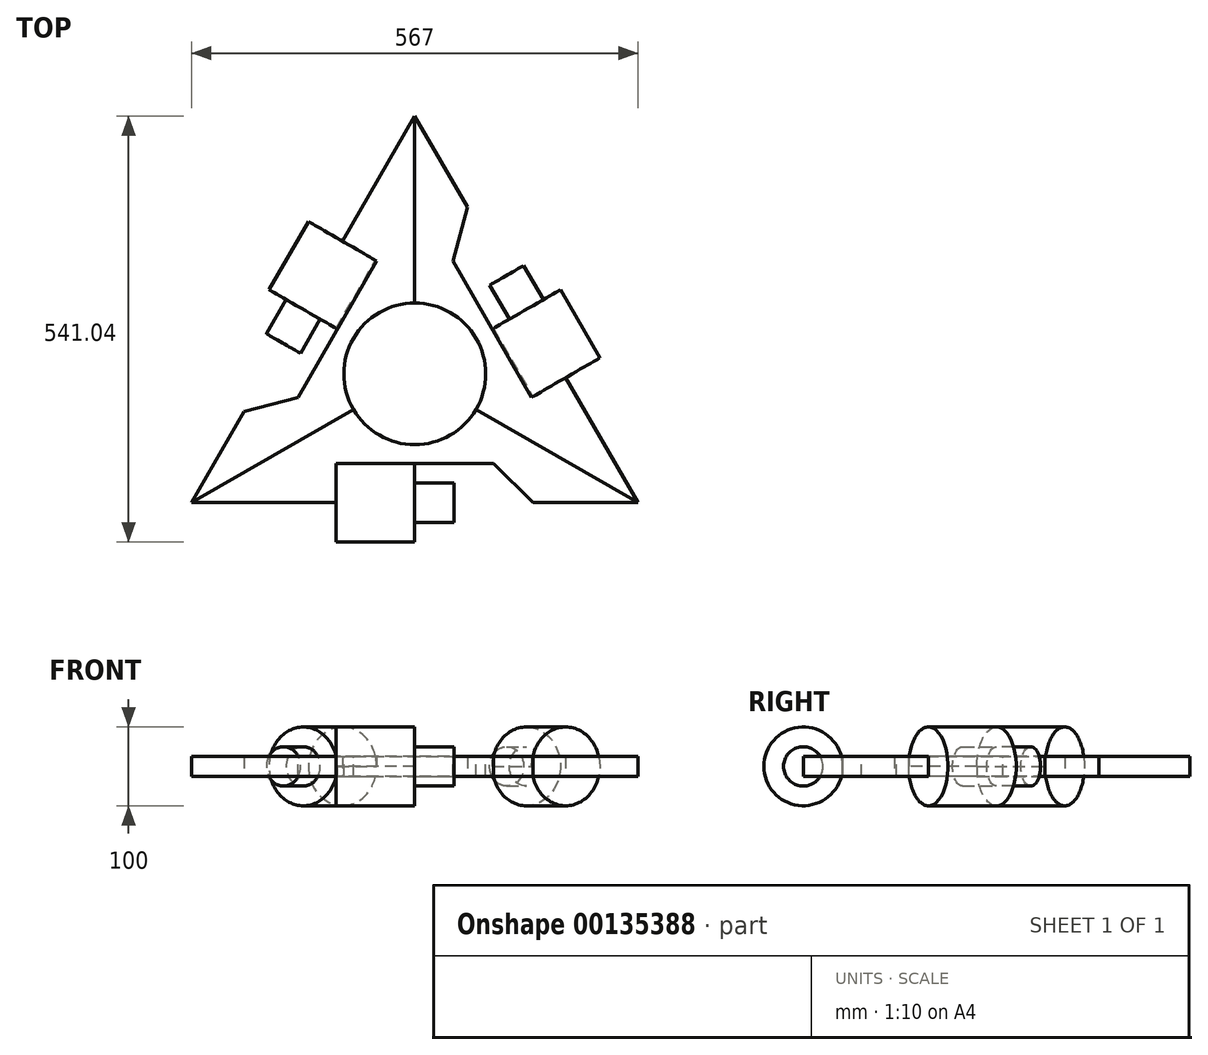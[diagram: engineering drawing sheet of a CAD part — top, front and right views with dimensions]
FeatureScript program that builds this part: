
annotation { "Feature Type Name" : "Feature", "Feature Type Description" : "" }
export const myFeature = defineFeature(function(context is Context, id is Id, definition is map)
    precondition{}
    {
        {
            var Q0;
            Q0=qCreatedBy(makeId("Top.planeOp"),FACE);
            var sketch = newSketch(context, id + "F0", { "sketchPlane" : qUnion([Q0])});
            skLineSegment(sketch, "E0", {"start": v(0, 0) * mm, "end": v(567, 0) * mm});
            skLineSegment(sketch, "E1", {"start": v(0, 0) * mm, "end": v(283.5, 491.04) * mm});
            skLineSegment(sketch, "E2", {"start": v(283.5, 491.04) * mm, "end": v(567, 0) * mm});
            skPoint(sketch, "E3", {"position": v(283.5, 491.04) * mm});
            skPoint(sketch, "E4", {"position": v(0, 0) * mm});
            skPoint(sketch, "E5", {"position": v(567, 0) * mm});
            skArc(sketch, "E6", {"start": v(567, 0) * mm, "mid": v(283.5, 491.04) * mm, "end": v(0, 0) * mm});
            skArc(sketch, "E7", {"start": v(283.5, 491.04) * mm, "mid": v(0, 0) * mm, "end": v(567, 0) * mm});
            skArc(sketch, "E8", {"start": v(0, 0) * mm, "mid": v(567, 0) * mm, "end": v(283.5, 491.04) * mm});
            skSolve(sketch);
        }
        {
            var Q0;
            Q0=makeQuery(id+"F0.imprint","IMPRINT",FACE,{"disambiguationData":[TD([[makeQuery(id+"F0.imprint","IMPRINT",EDGE,{"derivedFrom":sQuery(id+"F0.wireOp",EDGE,"E0")}),1.0]])]});
            extrude(context, id + "F1", {"entities" : qUnion([Q0]), "depth" : 25 * mm});
        }
        {
            var Q0;
            Q0=makeQuery(id+"F1.opExtrude","SWEPT_FACE",FACE,{"disambiguationData":[OSD([sQuery(id+"F0.wireOp",EDGE,"E0")])]});
            var sketch = newSketch(context, id + "F2", { "sketchPlane" : qUnion([Q0])});
            skLineSegment(sketch, "E9", {"start": v(0, 0) * mm, "end": v(567, 0) * mm});
            skLineSegment(sketch, "E10", {"start": v(283.5, 0) * mm, "end": v(283.5, 25) * mm});
            skLineSegment(sketch, "E11", {"start": v(283.5, 25) * mm, "end": v(383.5, 25) * mm});
            skLineSegment(sketch, "E12", {"start": v(383.5, 25) * mm, "end": v(383.5, 0) * mm});
            skLineSegment(sketch, "E13", {"start": v(383.5, 0) * mm, "end": v(283.5, 0) * mm});
            skLineSegment(sketch, "E14.bottom", {"start": v(283.5, 25) * mm, "end": v(183.5, 25) * mm});
            skLineSegment(sketch, "E14.top", {"start": v(283.5, 0) * mm, "end": v(183.5, 0) * mm});
            skLineSegment(sketch, "E14.left", {"start": v(283.5, 25) * mm, "end": v(283.5, 0) * mm});
            skLineSegment(sketch, "E14.right", {"start": v(183.5, 25) * mm, "end": v(183.5, 0) * mm});
            skSolve(sketch);
        }
        {
            var Q0;
            Q0=qSketchRegion(id+"F2",true);
            extrude(context, id + "F3", {"entities" : qUnion([Q0]), "operationType" : NewBodyOperationType.REMOVE, "oppositeDirection" : true, "depth" : 50 * mm});
        }
        {
            var Q0;
            Q0=makeQuery(id+"F3.boolean.opBoolean","COPY",FACE,{"derivedFrom":makeQuery(id+"F3.opExtrude","SWEPT_FACE",FACE,{"disambiguationData":[OSD([sQuery(id+"F2.wireOp",EDGE,"E14.right")])]})});
            var sketch = newSketch(context, id + "F4", { "sketchPlane" : qUnion([Q0])});
            skLineSegment(sketch, "E15", {"start": v(0, 0) * mm, "end": v(50, 0) * mm});
            skLineSegment(sketch, "E16", {"start": v(50, 0) * mm, "end": v(50, 25) * mm});
            skLineSegment(sketch, "E17", {"start": v(50, 12.5) * mm, "end": v(0, 12.5) * mm});
            skCircle(sketch, "E18", {"center": v(0, 12.5) * mm, "radius": 50 * mm});
            skSolve(sketch);
        }
        {
            var Q0;
            Q0=qSketchRegion(id+"F4",true);
            var Q1;
            {var subQ0=sQuery(id+"F2.wireOp",EDGE,"E14.right");var subQ1=makeQuery(id+"F3.boolean.opBoolean","COPY",EDGE,{"derivedFrom":makeQuery(id+"F3.opExtrude","CAP_EDGE",EDGE,{"disambiguationData":[OSD([subQ0])],"isStart":true})});var subQ7=sQuery(id+"F4.wireOp",EDGE,"E15");var subQ9=makeQuery(id+"F4.imprint","INTERSECT",VERTEX,{"derivedFrom":[subQ1,subQ7]});Q1=makeQuery(id+"F4.imprint","IMPRINT",FACE,{"disambiguationData":[TD([[makeQuery(id+"F4.imprint","IMPRINT",EDGE,{"disambiguationData":[TD([[subQ9,1.0]])],"derivedFrom":subQ7}),1.0]])]});}
            extrude(context, id + "F5", {"entities" : qUnion([Q0, Q1]), "operationType" : NewBodyOperationType.ADD, "depth" : 100 * mm});
        }
        {
            var Q0;
            Q0=makeQuery(id+"F5.opExtrude","CAP_FACE",FACE,{"disambiguationData":[OSD([sQuery(id+"F4.wireOp",EDGE,"E15"),sQuery(id+"F4.wireOp",EDGE,"E16"),sQuery(id+"F4.wireOp",EDGE,"E18")])],"isStart":false});
            var sketch = newSketch(context, id + "F6", { "sketchPlane" : qUnion([Q0])});
            skCircle(sketch, "E19", {"center": v(0, 12.5) * mm, "radius": 25 * mm});
            skSolve(sketch);
        }
        {
            var Q0;
            Q0=qSketchRegion(id+"F6",true);
            extrude(context, id + "F7", {"entities" : qUnion([Q0]), "operationType" : NewBodyOperationType.ADD, "depth" : 50 * mm});
        }
        {
            var Q0;
            Q0=makeQuery(id+"F3.boolean.opBoolean","COPY",FACE,{"derivedFrom":makeQuery(id+"F3.opExtrude","SWEPT_FACE",FACE,{"disambiguationData":[OSD([sQuery(id+"F2.wireOp",EDGE,"E12")])]})});
            extrude(context, id + "F8", {"entities" : qUnion([Q0]), "operationType" : NewBodyOperationType.REMOVE, "oppositeDirection" : true, "depth" : 50 * mm});
        }
        {
            var Q0;
            {var subQ0=sQuery(id+"F2.wireOp",EDGE,"E12");Q0=makeQuery(id+"F8.boolean.opBoolean","COPY",EDGE,{"derivedFrom":makeQuery(id+"F8.opExtrude","CAP_EDGE",EDGE,{"disambiguationData":[OSD([subQ0]),TDD([makeQuery(id+"F3.boolean.opBoolean","COPY",EDGE,{"derivedFrom":makeQuery(id+"F3.opExtrude","CAP_EDGE",EDGE,{"disambiguationData":[OSD([subQ0])],"isStart":true})})])],"isStart":false})});}
            chamfer(context, id + "F9", {"entities" : qUnion([Q0]), "width" : 50 * mm, "tangentPropagation" : true});
        }
        {
            var Q0;
            Q0=makeQuery(id+"F1.opExtrude","CAP_FACE",FACE,{"disambiguationData":[OSD([sQuery(id+"F0.wireOp",EDGE,"E0"),sQuery(id+"F0.wireOp",EDGE,"E1"),sQuery(id+"F0.wireOp",EDGE,"E2")])],"isStart":false});
            var sketch = newSketch(context, id + "F10", { "sketchPlane" : qUnion([Q0])});
            skLineSegment(sketch, "E20", {"start": v(567, 0) * mm, "end": v(141.75, 245.52) * mm});
            skLineSegment(sketch, "E21", {"start": v(0, 0) * mm, "end": v(425.25, 245.52) * mm});
            skCircle(sketch, "E22", {"center": v(283.5, 163.68) * mm, "radius": 90 * mm});
            skSolve(sketch);
        }
        {
            var Q0;
            Q0=qSketchRegion(id+"F10",true);
            var Q1;
            {var subQ1=makeQuery(id+"F1.opExtrude","CAP_EDGE",EDGE,{"disambiguationData":[OSD([sQuery(id+"F0.wireOp",EDGE,"E1")])],"isStart":false});var subQ3=sQuery(id+"F10.wireOp",EDGE,"E20");var subQ4=makeQuery(id+"F10.imprint","INTERSECT",VERTEX,{"derivedFrom":[subQ1,subQ3]});Q1=makeQuery(id+"F10.imprint","IMPRINT",FACE,{"disambiguationData":[TD([[makeQuery(id+"F10.imprint","IMPRINT",EDGE,{"disambiguationData":[TD([[subQ4,1.0]])],"derivedFrom":subQ3}),-1.0]])]});}
            var Q2;
            {var subQ2=sQuery(id+"F0.wireOp",EDGE,"E2");var subQ3=makeQuery(id+"F1.opExtrude","CAP_EDGE",EDGE,{"disambiguationData":[OSD([subQ2])],"isStart":false});var subQ7=sQuery(id+"F10.wireOp",EDGE,"E21");var subQ8=makeQuery(id+"F10.imprint","INTERSECT",VERTEX,{"derivedFrom":[subQ3,subQ7]});Q2=makeQuery(id+"F10.imprint","IMPRINT",FACE,{"disambiguationData":[TD([[makeQuery(id+"F10.imprint","IMPRINT",EDGE,{"disambiguationData":[TD([[subQ8,1.0]])],"derivedFrom":subQ7}),-1.0]])]});}
            var Q3;
            {var subQ0=sQuery(id+"F10.wireOp",EDGE,"E20");var subQ1=sQuery(id+"F0.wireOp",EDGE,"E1");var subQ2=makeQuery(id+"F1.opExtrude","CAP_EDGE",EDGE,{"disambiguationData":[OSD([subQ1])],"isStart":false});var subQ3=makeQuery(id+"F10.imprint","INTERSECT",VERTEX,{"derivedFrom":[subQ2,subQ0]});Q3=makeQuery(id+"F10.imprint","IMPRINT",FACE,{"disambiguationData":[TD([[makeQuery(id+"F10.imprint","IMPRINT",EDGE,{"disambiguationData":[TD([[subQ3,1.0]])],"derivedFrom":subQ0}),1.0]])]});}
            extrude(context, id + "F11", {"entities" : qUnion([Q0, Q1, Q2, Q3]), "operationType" : NewBodyOperationType.REMOVE, "oppositeDirection" : true, "depth" : 25 * mm});
        }
        {
            var Q0;
            Q0=makeQuery(id+"F1.opExtrude","CAP_FACE",FACE,{"disambiguationData":[OSD([sQuery(id+"F0.wireOp",EDGE,"E0"),sQuery(id+"F0.wireOp",EDGE,"E1"),sQuery(id+"F0.wireOp",EDGE,"E2")])],"isStart":false});
            var sketch = newSketch(context, id + "F12", { "sketchPlane" : qUnion([Q0])});
            skLineSegment(sketch, "E23", {"start": v(361.44, 118.68) * mm, "end": v(283.5, 163.68) * mm});
            skLineSegment(sketch, "E24", {"start": v(205.56, 118.68) * mm, "end": v(283.5, 163.68) * mm});
            skSolve(sketch);
        }
        {
            var Q0;
            Q0=qCreatedBy(makeId("Right.planeOp"),FACE);
            var Q1;
            Q1=sQuery(id+"F12.wireOp",VERTEX,"E24.end");
            cPlane(context, id + "F13", {"entities" : qUnion([Q0, Q1]), "cplaneType" : CPlaneType.PLANE_POINT, "offset" : 150 * mm, "width" : 150 * mm, "height" : 150 * mm});
        }
        {
            var Q0;
            Q0=qCreatedBy(id+"F13.planeOp",FACE);
            var sketch = newSketch(context, id + "F14", { "sketchPlane" : qUnion([Q0])});
            skPoint(sketch, "E25.0", {"position": v(163.68, 25) * mm});
            skLineSegment(sketch, "E26", {"start": v(163.68, 25) * mm, "end": v(163.68, -25) * mm});
            skSolve(sketch);
        }
        {
            var Q0;
            Q0=makeQuery(id+"F1.opExtrude","SWEPT_BODY",BODY,{"disambiguationData":[OSD([sQuery(id+"F0.wireOp",EDGE,"E0"),sQuery(id+"F0.wireOp",EDGE,"E1"),sQuery(id+"F0.wireOp",EDGE,"E2")])]});
            var Q1;
            Q1=sQuery(id+"F14.wireOp",EDGE,"E26");
            circularPattern(context, id + "F15", {"entities" : qUnion([Q0]), "axis" : qUnion([Q1]), "angle" : 120 * degree, "instanceCount" : 3});
        }
    });
